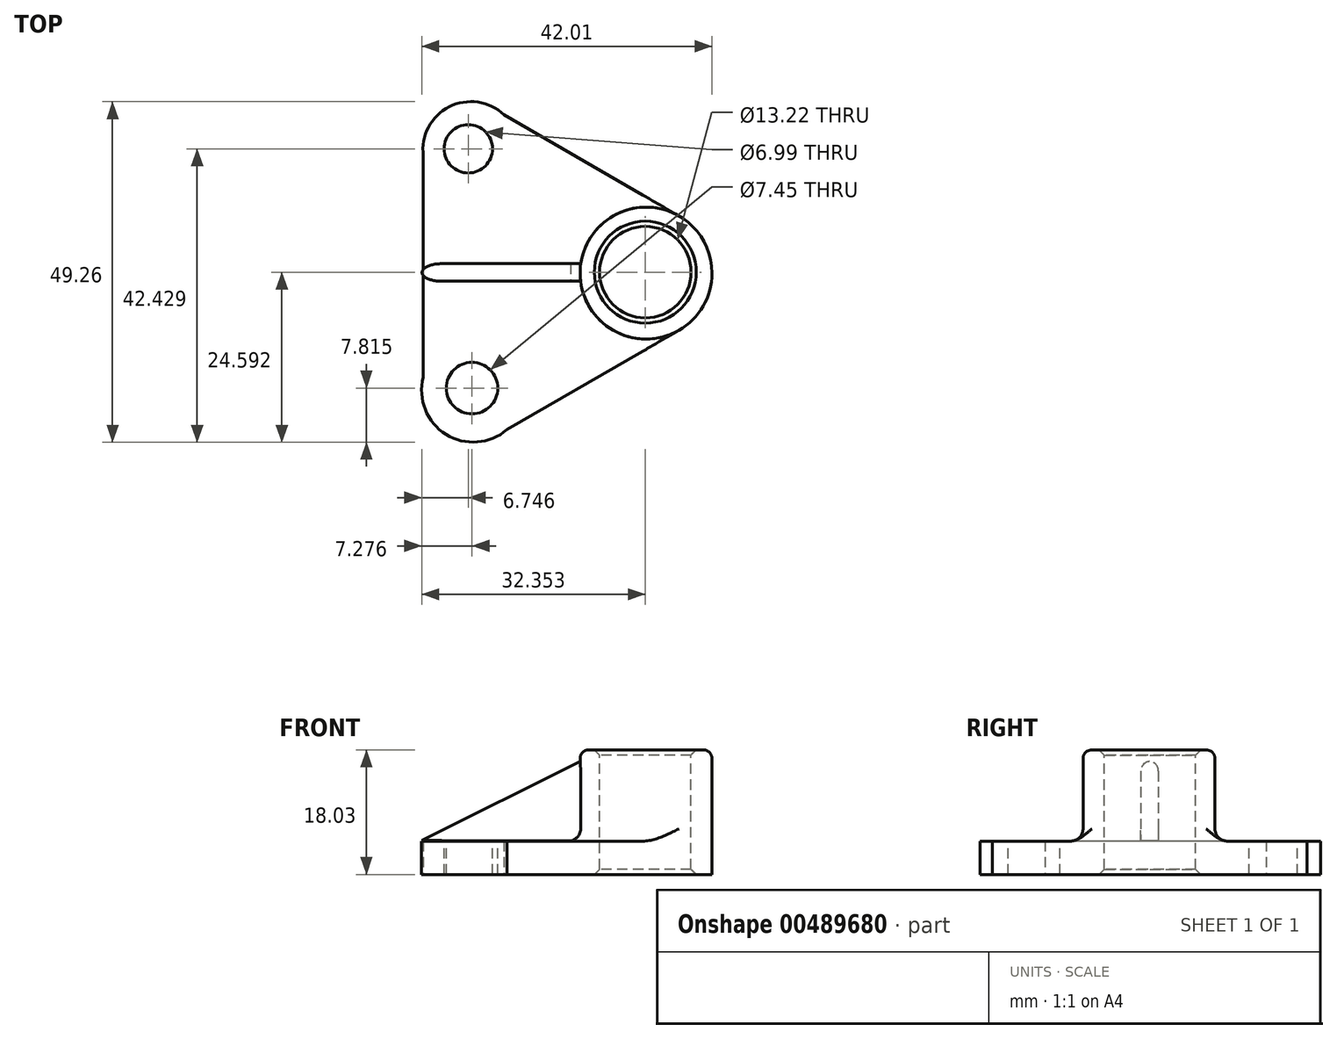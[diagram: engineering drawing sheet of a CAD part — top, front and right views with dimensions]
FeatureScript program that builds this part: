
annotation { "Feature Type Name" : "Feature", "Feature Type Description" : "" }
export const myFeature = defineFeature(function(context is Context, id is Id, definition is map)
    precondition{}
    {
        {
            var Q0;
            Q0=qCreatedBy(makeId("Top.planeOp"),FACE);
            var sketch = newSketch(context, id + "F0", { "sketchPlane" : qUnion([Q0])});
            skLineSegment(sketch, "E0", {"start": v(-34.96, 48.4) * mm, "end": v(-34.96, 10.73) * mm});
            skLineSegment(sketch, "E1", {"start": v(-25.28, 5.59) * mm, "end": v(2.04, 21.36) * mm});
            skLineSegment(sketch, "E2", {"start": v(2.04, 37.89) * mm, "end": v(-26.12, 54.15) * mm});
            skCircle(sketch, "E3", {"center": v(-2.73, 29.62) * mm, "radius": 9.54 * mm});
            skCircle(sketch, "E4", {"center": v(-27.73, 12.64) * mm, "radius": 7.47 * mm});
            skPoint(sketch, "E4.first.point", {"position": v(-25.28, 5.59) * mm});
            skPoint(sketch, "E4.second.point", {"position": v(-34.96, 10.73) * mm});
            skPoint(sketch, "E4.third.point", {"position": v(-20.27, 13.02) * mm});
            skCircle(sketch, "E5", {"center": v(-28.08, 47.49) * mm, "radius": 6.94 * mm});
            skPoint(sketch, "E5.first.point", {"position": v(-34.96, 48.4) * mm});
            skPoint(sketch, "E5.second.point", {"position": v(-21.34, 45.86) * mm});
            skPoint(sketch, "E5.third.point", {"position": v(-26.12, 54.15) * mm});
            skSolve(sketch);
        }
        {
            var Q0;
            Q0 = qSketchRegion(id + "F0", true);
            extrude(context, id + "F1", {"entities" : qUnion([Q0]), "depth" : 4.83 * mm});
        }
        {
            var Q0;
            {var subQ0=sQuery(id+"F0.wireOp",EDGE,"E3");var subQ1=makeQuery(id+"F0.imprint","INTERSECT",VERTEX,{"derivedFrom":[sQuery(id+"F0.wireOp",EDGE,"E1"),subQ0]});Q0=makeQuery(id+"F0.imprint","IMPRINT",FACE,{"disambiguationData":[TD([[makeQuery(id+"F0.imprint","IMPRINT",EDGE,{"disambiguationData":[TD([[subQ1,1.0]])],"derivedFrom":subQ0}),1.0]])]});}
            var Q1;
            Q1=sQuery(id+"F0.wireOp",EDGE,"E3");
            extrude(context, id + "F2", {"entities" : qUnion([Q0]), "operationType" : NewBodyOperationType.ADD, "surfaceEntities" : qUnion([Q1]), "depth" : 18.03 * mm});
        }
        {
            var Q0;
            Q0=qCreatedBy(makeId("Top.planeOp"),FACE);
            cPlane(context, id + "F3", {"entities" : qUnion([Q0]), "cplaneType" : CPlaneType.OFFSET, "offset" : 32.5 * mm, "width" : 152.4 * mm, "height" : 152.4 * mm});
        }
        {
            var Q0;
            Q0=qCreatedBy(id+"F3.planeOp",FACE);
            var sketch = newSketch(context, id + "F4", { "sketchPlane" : qUnion([Q0])});
            skCircle(sketch, "E6", {"center": v(-2.85, 29.76) * mm, "radius": 6.61 * mm});
            skCircle(sketch, "E7", {"center": v(-28.45, 47.6) * mm, "radius": 3.5 * mm});
            skCircle(sketch, "E8", {"center": v(-27.92, 12.99) * mm, "radius": 3.73 * mm});
            skSolve(sketch);
        }
        {
            var Q0;
            Q0=makeQuery(id+"F4.imprint","IMPRINT",FACE,{"disambiguationData":[TD([[makeQuery(id+"F4.imprint","IMPRINT",EDGE,{"derivedFrom":sQuery(id+"F4.wireOp",EDGE,"E6")}),1.0]])]});
            var Q1;
            Q1=makeQuery(id+"F4.imprint","IMPRINT",FACE,{"disambiguationData":[TD([[makeQuery(id+"F4.imprint","IMPRINT",EDGE,{"derivedFrom":sQuery(id+"F4.wireOp",EDGE,"E8")}),1.0]])]});
            var Q2;
            Q2=makeQuery(id+"F4.imprint","IMPRINT",FACE,{"disambiguationData":[TD([[makeQuery(id+"F4.imprint","IMPRINT",EDGE,{"derivedFrom":sQuery(id+"F4.wireOp",EDGE,"E7")}),1.0]])]});
            extrude(context, id + "F5", {"entities" : qUnion([Q0, Q1, Q2]), "operationType" : NewBodyOperationType.REMOVE, "oppositeDirection" : true, "depth" : 49.28 * mm});
        }
        {
            var Q0;
            Q0=makeQuery(id+"F5.boolean.opBoolean","INTERSECT",EDGE,{"derivedFrom":[makeQuery(id+"F2.opExtrude","CAP_FACE",FACE,{"disambiguationData":[OSD([sQuery(id+"F0.wireOp",EDGE,"E3")])],"isStart":false}),makeQuery(id+"F5.opExtrude","SWEPT_FACE",FACE,{"disambiguationData":[OSD([sQuery(id+"F4.wireOp",EDGE,"E6")])]})]});
            chamfer(context, id + "F6", {"entities" : qUnion([Q0]), "width" : 0.76 * mm, "tangentPropagation" : true});
        }
        {
            var Q0;
            Q0=makeQuery(id+"F2.opExtrude","CAP_EDGE",EDGE,{"disambiguationData":[OSD([sQuery(id+"F0.wireOp",EDGE,"E3")])],"isStart":false});
            fillet(context, id + "F7", {"entities" : qUnion([Q0]), "radius" : 1.27 * mm, "tangentPropagation" : true, "allowEdgeOverflow" : false});
        }
        {
            var Q0;
            Q0=makeQuery(id+"F5.boolean.opBoolean","INTERSECT",EDGE,{"derivedFrom":[makeQuery(id+"F1.opExtrude","CAP_FACE",FACE,{"disambiguationData":[OSD([sQuery(id+"F0.wireOp",EDGE,"E0"),sQuery(id+"F0.wireOp",EDGE,"E1"),sQuery(id+"F0.wireOp",EDGE,"E2"),sQuery(id+"F0.wireOp",EDGE,"E3"),sQuery(id+"F0.wireOp",EDGE,"E4"),sQuery(id+"F0.wireOp",EDGE,"E5")])],"isStart":true}),makeQuery(id+"F5.opExtrude","SWEPT_FACE",FACE,{"disambiguationData":[OSD([sQuery(id+"F4.wireOp",EDGE,"E6")])]})]});
            chamfer(context, id + "F8", {"entities" : qUnion([Q0]), "width" : 0.76 * mm, "tangentPropagation" : true});
        }
        {
            var Q0;
            Q0=qCreatedBy(makeId("Front.planeOp"),FACE);
            cPlane(context, id + "F9", {"entities" : qUnion([Q0]), "cplaneType" : CPlaneType.OFFSET, "offset" : 29.72 * mm, "oppositeDirection" : true, "width" : 152.4 * mm, "height" : 152.4 * mm});
        }
        {
            var Q0;
            Q0=qCreatedBy(id+"F9.planeOp",FACE);
            var sketch = newSketch(context, id + "F10", { "sketchPlane" : qUnion([Q0])});
            skLineSegment(sketch, "E9", {"start": v(-11.42, 16.76) * mm, "end": v(-35.16, 4.93) * mm});
            skLineSegment(sketch, "E10", {"start": v(-11.42, 16.76) * mm, "end": v(-11.42, 4.86) * mm});
            skLineSegment(sketch, "E11", {"start": v(-11.42, 4.86) * mm, "end": v(-35.16, 4.93) * mm});
            skSolve(sketch);
        }
        {
            var Q0;
            Q0 = qSketchRegion(id + "F10", true);
            extrude(context, id + "F11", {"entities" : qUnion([Q0]), "operationType" : NewBodyOperationType.ADD, "endBound" : BoundingType.SYMMETRIC, "depth" : 2.54 * mm});
        }
        {
            var Q0;
            Q0=makeQuery(id+"F11.opExtrude","CAP_EDGE",EDGE,{"disambiguationData":[OSD([sQuery(id+"F10.wireOp",EDGE,"E9")])],"isStart":true});
            fillet(context, id + "F12", {"entities" : qUnion([Q0]), "radius" : 1.27 * mm, "tangentPropagation" : true, "allowEdgeOverflow" : false});
        }
        {
            var Q0;
            Q0=makeQuery(id+"F11.opExtrude","CAP_EDGE",EDGE,{"disambiguationData":[OSD([sQuery(id+"F10.wireOp",EDGE,"E9")])],"isStart":false});
            fillet(context, id + "F13", {"entities" : qUnion([Q0]), "radius" : 1.27 * mm, "tangentPropagation" : true, "allowEdgeOverflow" : false});
        }
        {
            var Q0;
            {var subQ0=sQuery(id+"F0.wireOp",EDGE,"E3");Q0=makeQuery(id+"F2.boolean.opBoolean","INTERSECT",EDGE,{"derivedFrom":[makeQuery(id+"F1.opExtrude","CAP_FACE",FACE,{"disambiguationData":[OSD([sQuery(id+"F0.wireOp",EDGE,"E0"),sQuery(id+"F0.wireOp",EDGE,"E1"),sQuery(id+"F0.wireOp",EDGE,"E2"),subQ0,sQuery(id+"F0.wireOp",EDGE,"E4"),sQuery(id+"F0.wireOp",EDGE,"E5")])],"isStart":false}),makeQuery(id+"F2.opExtrude","SWEPT_FACE",FACE,{"disambiguationData":[OSD([subQ0])]})]});}
            fillet(context, id + "F14", {"entities" : qUnion([Q0]), "radius" : 1.78 * mm, "tangentPropagation" : true, "allowEdgeOverflow" : false});
        }
    });
